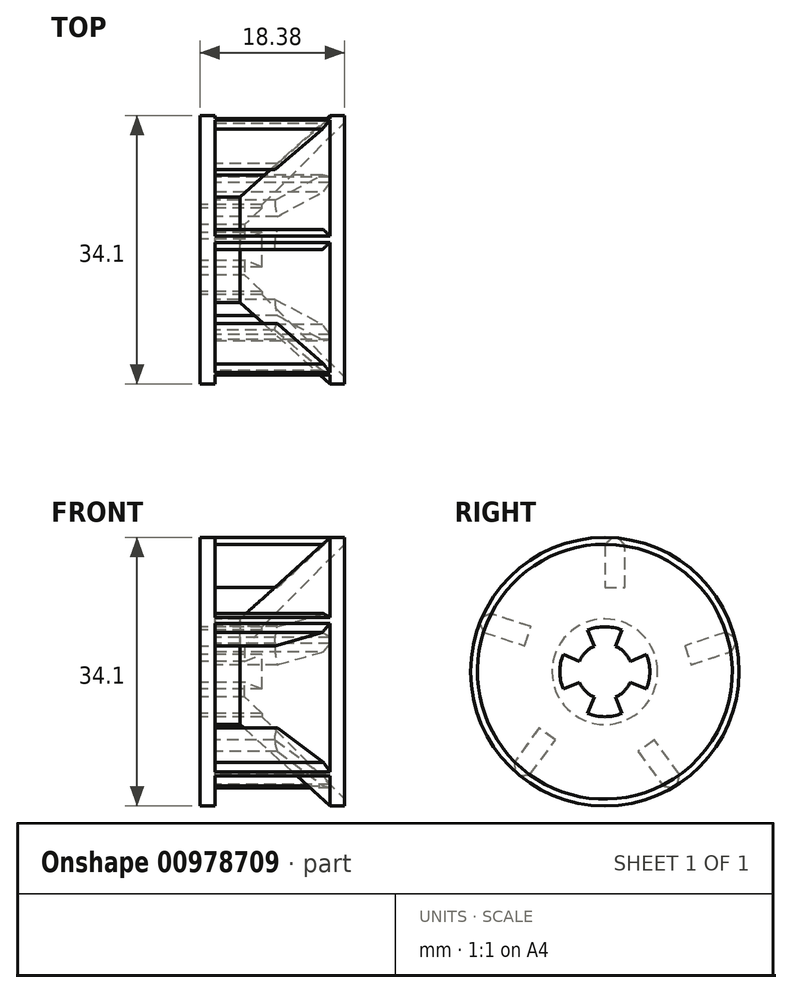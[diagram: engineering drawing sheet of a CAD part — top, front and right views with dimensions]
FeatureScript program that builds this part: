
annotation { "Feature Type Name" : "Feature", "Feature Type Description" : "" }
export const myFeature = defineFeature(function(context is Context, id is Id, definition is map)
    precondition{}
    {
        {
            var Q0;
            Q0=qCreatedBy(makeId("Front.planeOp"),FACE);
            var sketch = newSketch(context, id + "F0", { "sketchPlane" : qUnion([Q0])});
            skPoint(sketch, "E0", {"position": v(16.68, 17.05) * mm});
            skLineSegment(sketch, "E1", {"start": v(0, 0) * mm, "end": v(7.84, 0) * mm});
            skLineSegment(sketch, "E2", {"start": v(2.04, 6.7) * mm, "end": v(5.21, 6.7) * mm});
            skLineSegment(sketch, "E3", {"start": v(16.68, 17.05) * mm, "end": v(5.21, 6.7) * mm});
            skPoint(sketch, "E4.visualSharp", {"position": v(2.04, 17.05) * mm});
            skLineSegment(sketch, "E5", {"start": v(2.04, 6.7) * mm, "end": v(2.04, 17.05) * mm});
            skLineSegment(sketch, "E6", {"start": v(0.13, 17.05) * mm, "end": v(2.04, 17.05) * mm});
            skLineSegment(sketch, "E7", {"start": v(18.51, 16.19) * mm, "end": v(18.51, 17.05) * mm});
            skLineSegment(sketch, "E8", {"start": v(18.51, 17.05) * mm, "end": v(16.68, 17.05) * mm});
            skLineSegment(sketch, "E9", {"start": v(0.13, 3.5) * mm, "end": v(5.82, 3.5) * mm});
            skLineSegment(sketch, "E10", {"start": v(5.82, 3.5) * mm, "end": v(18.51, 16.19) * mm});
            skLineSegment(sketch, "E11", {"start": v(0.13, 17.05) * mm, "end": v(0.13, 3.5) * mm});
            skSolve(sketch);
        }
        {
            var Q0;
            Q0=makeQuery(id+"F0.imprint","IMPRINT",FACE,{"disambiguationData":[TD([[makeQuery(id+"F0.imprint","IMPRINT",EDGE,{"derivedFrom":sQuery(id+"F0.wireOp",EDGE,"E2")}),-1.0]])]});
            var Q1;
            Q1=sQuery(id+"F0.wireOp",EDGE,"E1");
            revolve(context, id + "F1", {"entities" : qUnion([Q0]), "axis" : qUnion([Q1]), "revolveType" : RevolveType.FULL});
        }
        {
            var Q0;
            Q0=makeQuery(id+"F1.opRevolve","SWEPT_FACE",FACE,{"disambiguationData":[OSD([sQuery(id+"F0.wireOp",EDGE,"E11")])]});
            var sketch = newSketch(context, id + "F2", { "sketchPlane" : qUnion([Q0])});
            skArc(sketch, "E12", {"start": v(3.23, -1.34) * mm, "mid": v(3.5, 0) * mm, "end": v(3.23, 1.34) * mm});
            skArc(sketch, "E13", {"start": v(-1.34, -3.23) * mm, "mid": v(0, -3.5) * mm, "end": v(1.34, -3.23) * mm});
            skArc(sketch, "E14", {"start": v(-3.23, 1.34) * mm, "mid": v(-3.5, 0) * mm, "end": v(-3.23, -1.34) * mm});
            skArc(sketch, "E15", {"start": v(1.34, 3.23) * mm, "mid": v(0, 3.5) * mm, "end": v(-1.34, 3.23) * mm});
            skLineSegment(sketch, "E16", {"start": v(-5.28, 2.19) * mm, "end": v(-3.23, 1.34) * mm});
            skLineSegment(sketch, "E17", {"start": v(-1.34, 3.23) * mm, "end": v(-2.19, 5.28) * mm});
            skLineSegment(sketch, "E18", {"start": v(2.19, 5.28) * mm, "end": v(1.34, 3.23) * mm});
            skLineSegment(sketch, "E19", {"start": v(3.23, 1.34) * mm, "end": v(5.28, 2.19) * mm});
            skLineSegment(sketch, "E20", {"start": v(3.23, -1.34) * mm, "end": v(5.28, -2.19) * mm});
            skLineSegment(sketch, "E21", {"start": v(1.34, -3.23) * mm, "end": v(2.19, -5.28) * mm});
            skLineSegment(sketch, "E22", {"start": v(-1.34, -3.23) * mm, "end": v(-2.19, -5.28) * mm});
            skLineSegment(sketch, "E23", {"start": v(-3.23, -1.34) * mm, "end": v(-5.28, -2.19) * mm});
            skArc(sketch, "E24", {"start": v(-5.28, 2.19) * mm, "mid": v(-5.72, 0) * mm, "end": v(-5.28, -2.19) * mm});
            skArc(sketch, "E25", {"start": v(-2.19, -5.28) * mm, "mid": v(0, -5.72) * mm, "end": v(2.19, -5.28) * mm});
            skArc(sketch, "E26", {"start": v(5.28, -2.19) * mm, "mid": v(5.72, 0) * mm, "end": v(5.28, 2.19) * mm});
            skArc(sketch, "E27", {"start": v(2.19, 5.28) * mm, "mid": v(0, 5.72) * mm, "end": v(-2.19, 5.28) * mm});
            skSolve(sketch);
        }
        {
            var Q0;
            Q0=qSketchRegion(id+"F2",true);
            extrude(context, id + "F3", {"entities" : qUnion([Q0]), "operationType" : NewBodyOperationType.REMOVE, "endBound" : BoundingType.UP_TO_NEXT, "oppositeDirection" : true, "depth" : 25.4 * mm});
        }
        {
            var Q0;
            Q0=makeQuery(id+"F1.opRevolve","SWEPT_FACE",FACE,{"disambiguationData":[OSD([sQuery(id+"F0.wireOp",EDGE,"E5")])]});
            var sketch = newSketch(context, id + "F4", { "sketchPlane" : qUnion([Q0])});
            skLineSegment(sketch, "E28", {"start": v(0, 17.05) * mm, "end": v(0, 10.7) * mm});
            skLineSegment(sketch, "E29", {"start": v(0, 10.7) * mm, "end": v(2.54, 10.7) * mm});
            skLineSegment(sketch, "E30", {"start": v(2.54, 10.7) * mm, "end": v(2.54, 16.86) * mm});
            skLineSegment(sketch, "E31.1.0", {"start": v(-16.22, 5.27) * mm, "end": v(-10.18, 3.3) * mm});
            skLineSegment(sketch, "E31.1.1", {"start": v(-10.18, 3.3) * mm, "end": v(-9.4, 5.72) * mm});
            skLineSegment(sketch, "E31.1.2", {"start": v(-9.4, 5.72) * mm, "end": v(-15.25, 7.63) * mm});
            skLineSegment(sketch, "E31.2.0", {"start": v(-10.02, -13.8) * mm, "end": v(-6.29, -8.66) * mm});
            skLineSegment(sketch, "E31.2.1", {"start": v(-6.29, -8.66) * mm, "end": v(-8.34, -7.16) * mm});
            skLineSegment(sketch, "E31.2.2", {"start": v(-8.34, -7.16) * mm, "end": v(-11.97, -12.15) * mm});
            skPoint(sketch, "E31.center", {"position": v(0, 0) * mm});
            skLineSegment(sketch, "E32.2.3.0", {"start": v(10.02, -13.8) * mm, "end": v(6.29, -8.66) * mm});
            skLineSegment(sketch, "E32.3.3.0", {"start": v(6.29, -8.66) * mm, "end": v(4.23, -10.15) * mm});
            skLineSegment(sketch, "E32.6.3.0", {"start": v(4.23, -10.15) * mm, "end": v(7.86, -15.13) * mm});
            skLineSegment(sketch, "E32.2.4.0", {"start": v(16.22, 5.27) * mm, "end": v(10.18, 3.3) * mm});
            skLineSegment(sketch, "E32.3.4.0", {"start": v(10.18, 3.3) * mm, "end": v(10.96, 0.9) * mm});
            skLineSegment(sketch, "E32.6.4.0", {"start": v(10.96, 0.9) * mm, "end": v(16.82, 2.8) * mm});
            skSolve(sketch);
        }
        {
            var Q0;
            {var subQ0=sQuery(id+"F4.wireOp",EDGE,"E32.2.4.0");Q0=makeQuery(id+"F4.imprint","IMPRINT",FACE,{"disambiguationData":[TD([[makeQuery(id+"F4.imprint","IMPRINT",EDGE,{"derivedFrom":subQ0}),1.0]])]});}
            var Q1;
            {var subQ0=sQuery(id+"F4.wireOp",EDGE,"E32.2.3.0");Q1=makeQuery(id+"F4.imprint","IMPRINT",FACE,{"disambiguationData":[TD([[makeQuery(id+"F4.imprint","IMPRINT",EDGE,{"derivedFrom":subQ0}),1.0]])]});}
            var Q2;
            {var subQ0=sQuery(id+"F4.wireOp",EDGE,"E28");Q2=makeQuery(id+"F4.imprint","IMPRINT",FACE,{"disambiguationData":[TD([[makeQuery(id+"F4.imprint","IMPRINT",EDGE,{"derivedFrom":subQ0}),1.0]])]});}
            var Q3;
            {var subQ0=sQuery(id+"F4.wireOp",EDGE,"E31.1.0");Q3=makeQuery(id+"F4.imprint","IMPRINT",FACE,{"disambiguationData":[TD([[makeQuery(id+"F4.imprint","IMPRINT",EDGE,{"derivedFrom":subQ0}),1.0]])]});}
            var Q4;
            {var subQ0=sQuery(id+"F4.wireOp",EDGE,"E31.2.0");Q4=makeQuery(id+"F4.imprint","IMPRINT",FACE,{"disambiguationData":[TD([[makeQuery(id+"F4.imprint","IMPRINT",EDGE,{"derivedFrom":subQ0}),1.0]])]});}
            var Q5;
            Q5=makeQuery(id+"F1.opRevolve","SWEPT_FACE",FACE,{"disambiguationData":[OSD([sQuery(id+"F0.wireOp",EDGE,"E3")])]});
            extrude(context, id + "F5", {"entities" : qUnion([Q0, Q1, Q2, Q3, Q4]), "operationType" : NewBodyOperationType.ADD, "endBound" : BoundingType.UP_TO_SURFACE, "depth" : 25.4 * mm, "endBoundEntityFace" : qUnion([Q5]), "offsetDistance" : 25.4 * mm});
        }
        {
            var Q0;
            Q0=makeQuery(id+"F5.opExtrude","SWEPT_EDGE",EDGE,{"disambiguationData":[OSD([sQuery(id+"F0.wireOp",EDGE,"E5"),sQuery(id+"F0.wireOp",EDGE,"E6"),sQuery(id+"F4.wireOp",EDGE,"E31.2.2")])]});
            var Q1;
            Q1=makeQuery(id+"F5.opExtrude","SWEPT_EDGE",EDGE,{"disambiguationData":[OSD([sQuery(id+"F0.wireOp",EDGE,"E5"),sQuery(id+"F0.wireOp",EDGE,"E6"),sQuery(id+"F4.wireOp",EDGE,"E31.2.0")])]});
            var Q2;
            Q2=makeQuery(id+"F5.opExtrude","SWEPT_EDGE",EDGE,{"disambiguationData":[OSD([sQuery(id+"F0.wireOp",EDGE,"E5"),sQuery(id+"F0.wireOp",EDGE,"E6"),sQuery(id+"F4.wireOp",EDGE,"E31.1.0")])]});
            var Q3;
            Q3=makeQuery(id+"F5.opExtrude","SWEPT_EDGE",EDGE,{"disambiguationData":[OSD([sQuery(id+"F0.wireOp",EDGE,"E5"),sQuery(id+"F0.wireOp",EDGE,"E6"),sQuery(id+"F4.wireOp",EDGE,"E31.1.2")])]});
            var Q4;
            Q4=makeQuery(id+"F5.opExtrude","SWEPT_EDGE",EDGE,{"disambiguationData":[OSD([sQuery(id+"F0.wireOp",EDGE,"E5"),sQuery(id+"F0.wireOp",EDGE,"E6"),sQuery(id+"F4.wireOp",EDGE,"E30")])]});
            var Q5;
            Q5=makeQuery(id+"F5.opExtrude","SWEPT_EDGE",EDGE,{"disambiguationData":[OSD([sQuery(id+"F0.wireOp",EDGE,"E5"),sQuery(id+"F0.wireOp",EDGE,"E6"),sQuery(id+"F4.wireOp",EDGE,"E28")])]});
            var Q6;
            Q6=makeQuery(id+"F5.opExtrude","SWEPT_EDGE",EDGE,{"disambiguationData":[OSD([sQuery(id+"F0.wireOp",EDGE,"E5"),sQuery(id+"F0.wireOp",EDGE,"E6"),sQuery(id+"F4.wireOp",EDGE,"E32.2.4.0")])]});
            var Q7;
            Q7=makeQuery(id+"F5.opExtrude","SWEPT_EDGE",EDGE,{"disambiguationData":[OSD([sQuery(id+"F0.wireOp",EDGE,"E5"),sQuery(id+"F0.wireOp",EDGE,"E6"),sQuery(id+"F4.wireOp",EDGE,"E32.6.4.0")])]});
            var Q8;
            Q8=makeQuery(id+"F5.opExtrude","SWEPT_EDGE",EDGE,{"disambiguationData":[OSD([sQuery(id+"F0.wireOp",EDGE,"E5"),sQuery(id+"F0.wireOp",EDGE,"E6"),sQuery(id+"F4.wireOp",EDGE,"E32.2.3.0")])]});
            var Q9;
            Q9=makeQuery(id+"F5.opExtrude","SWEPT_EDGE",EDGE,{"disambiguationData":[OSD([sQuery(id+"F0.wireOp",EDGE,"E5"),sQuery(id+"F0.wireOp",EDGE,"E6"),sQuery(id+"F4.wireOp",EDGE,"E32.6.3.0")])]});
            chamfer(context, id + "F6", {"entities" : qUnion([Q0, Q1, Q2, Q3, Q4, Q5, Q6, Q7, Q8, Q9]), "width" : 0.89 * mm, "tangentPropagation" : true});
        }
    });
